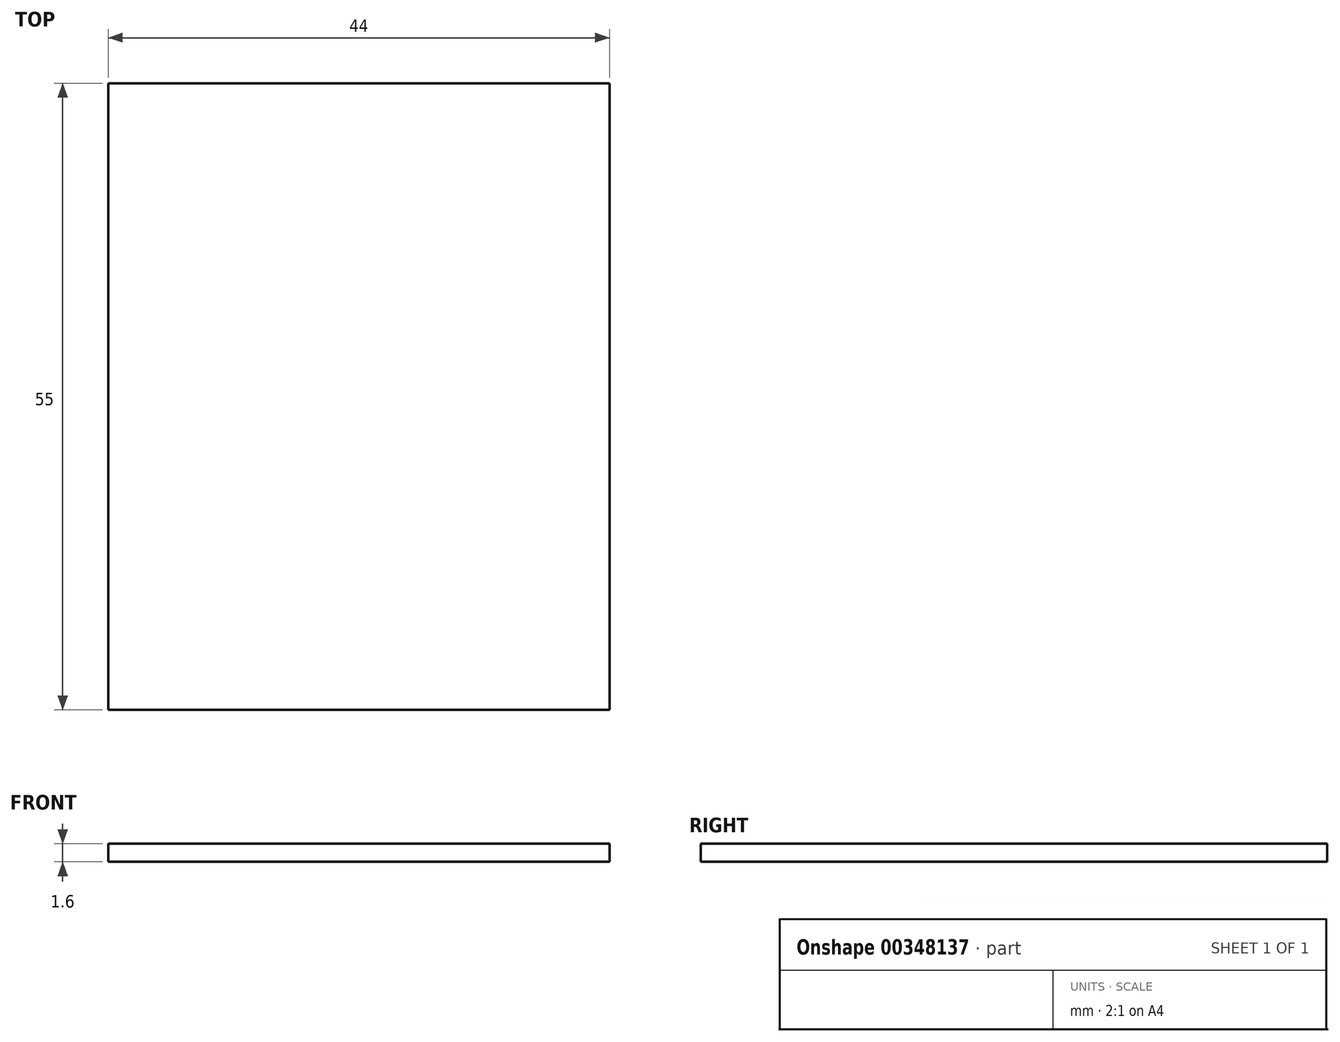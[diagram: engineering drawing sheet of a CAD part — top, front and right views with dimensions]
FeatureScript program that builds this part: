
annotation { "Feature Type Name" : "Feature", "Feature Type Description" : "" }
export const myFeature = defineFeature(function(context is Context, id is Id, definition is map)
    precondition{}
    {
        {
            var Q0;
            Q0=qCreatedBy(makeId("Top.planeOp"),FACE);
            var sketch = newSketch(context, id + "F0", { "sketchPlane" : qUnion([Q0])});
            skLineSegment(sketch, "E0.bottom", {"start": v(22, 27.5) * mm, "end": v(-22, 27.5) * mm});
            skLineSegment(sketch, "E0.top", {"start": v(22, -27.5) * mm, "end": v(-22, -27.5) * mm});
            skLineSegment(sketch, "E0.left", {"start": v(22, 27.5) * mm, "end": v(22, -27.5) * mm});
            skLineSegment(sketch, "E0.right", {"start": v(-22, 27.5) * mm, "end": v(-22, -27.5) * mm});
            skPoint(sketch, "E0.middle", {"position": v(0, 0) * mm});
            skSolve(sketch);
        }
        {
            var Q0;
            Q0=makeQuery(id+"F0.imprint","IMPRINT",FACE,{"disambiguationData":[TD([[makeQuery(id+"F0.imprint","IMPRINT",EDGE,{"derivedFrom":sQuery(id+"F0.wireOp",EDGE,"E0.bottom")}),1.0]])]});
            extrude(context, id + "F1", {"entities" : qUnion([Q0]), "depth" : 1.6 * mm});
        }
    });
